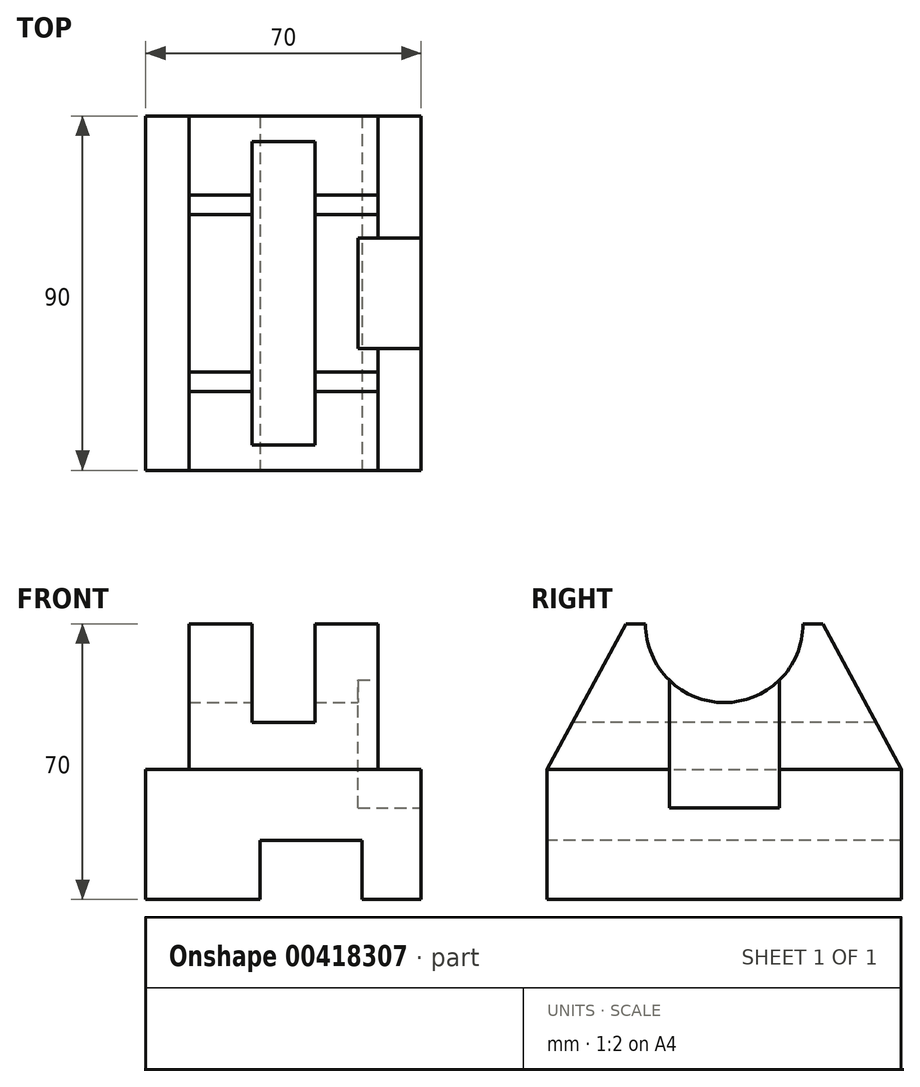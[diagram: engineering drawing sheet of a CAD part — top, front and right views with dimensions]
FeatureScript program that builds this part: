
annotation { "Feature Type Name" : "Feature", "Feature Type Description" : "" }
export const myFeature = defineFeature(function(context is Context, id is Id, definition is map)
    precondition{}
    {
        {
            var Q0;
            Q0=qCreatedBy(makeId("Right.planeOp"),FACE);
            var sketch = newSketch(context, id + "F0", { "sketchPlane" : qUnion([Q0])});
            skLineSegment(sketch, "E0", {"start": v(-45, 0) * mm, "end": v(45, 0) * mm});
            skLineSegment(sketch, "E1", {"start": v(45, 0) * mm, "end": v(25, 37) * mm});
            skLineSegment(sketch, "E2", {"start": v(25, 37) * mm, "end": v(-25, 37) * mm});
            skLineSegment(sketch, "E3", {"start": v(-25, 37) * mm, "end": v(-45, 0) * mm});
            skSolve(sketch);
        }
        {
            var Q0;
            Q0=qCreatedBy(makeId("Top.planeOp"),FACE);
            var sketch = newSketch(context, id + "F1", { "sketchPlane" : qUnion([Q0])});
            skLineSegment(sketch, "E4.bottom", {"start": v(-35, -45) * mm, "end": v(35, -45) * mm});
            skLineSegment(sketch, "E4.top", {"start": v(-35, 45) * mm, "end": v(35, 45) * mm});
            skLineSegment(sketch, "E4.left", {"start": v(-35, -45) * mm, "end": v(-35, 45) * mm});
            skLineSegment(sketch, "E4.right", {"start": v(35, -45) * mm, "end": v(35, 45) * mm});
            skPoint(sketch, "E4.middle", {"position": v(0, 0) * mm});
            skSolve(sketch);
        }
        {
            var Q0;
            Q0 = qSketchRegion(id + "F1", true);
            extrude(context, id + "F2", {"entities" : qUnion([Q0]), "oppositeDirection" : true, "depth" : 33 * mm});
        }
        {
            var Q0;
            Q0=makeQuery(id+"F2.opExtrude","SWEPT_FACE",FACE,{"disambiguationData":[OSD([sQuery(id+"F1.wireOp",EDGE,"E4.bottom")])]});
            var sketch = newSketch(context, id + "F3", { "sketchPlane" : qUnion([Q0])});
            skLineSegment(sketch, "E5.bottom", {"start": v(-6, -18) * mm, "end": v(20, -18) * mm});
            skLineSegment(sketch, "E5.top", {"start": v(-6, -33) * mm, "end": v(20, -33) * mm});
            skLineSegment(sketch, "E5.left", {"start": v(-6, -18) * mm, "end": v(-6, -33) * mm});
            skLineSegment(sketch, "E5.right", {"start": v(20, -18) * mm, "end": v(20, -33) * mm});
            skSolve(sketch);
        }
        {
            var Q0;
            Q0 = qSketchRegion(id + "F3", true);
            extrude(context, id + "F4", {"entities" : qUnion([Q0]), "operationType" : NewBodyOperationType.REMOVE, "endBound" : BoundingType.THROUGH_ALL, "oppositeDirection" : true, "depth" : 25 * mm});
        }
        {
            var Q0;
            Q0 = qSketchRegion(id + "F0", true);
            extrude(context, id + "F5", {"entities" : qUnion([Q0]), "operationType" : NewBodyOperationType.ADD, "endBound" : BoundingType.SYMMETRIC, "depth" : 48 * mm});
        }
        {
            var Q0;
            Q0=makeQuery(id+"F2.opExtrude","SWEPT_FACE",FACE,{"disambiguationData":[OSD([sQuery(id+"F1.wireOp",EDGE,"E4.bottom")])]});
            var sketch = newSketch(context, id + "F6", { "sketchPlane" : qUnion([Q0])});
            skLineSegment(sketch, "E6.bottom", {"start": v(-8, 37) * mm, "end": v(8, 37) * mm});
            skLineSegment(sketch, "E6.top", {"start": v(-8, 12) * mm, "end": v(8, 12) * mm});
            skLineSegment(sketch, "E6.left", {"start": v(-8, 37) * mm, "end": v(-8, 12) * mm});
            skLineSegment(sketch, "E6.right", {"start": v(8, 37) * mm, "end": v(8, 12) * mm});
            skSolve(sketch);
        }
        {
            var Q0;
            Q0 = qSketchRegion(id + "F6", true);
            extrude(context, id + "F7", {"entities" : qUnion([Q0]), "operationType" : NewBodyOperationType.REMOVE, "endBound" : BoundingType.THROUGH_ALL, "oppositeDirection" : true, "depth" : 25 * mm});
        }
        {
            var Q0;
            Q0=makeQuery(id+"F5.opExtrude","CAP_FACE",FACE,{"disambiguationData":[OSD([sQuery(id+"F0.wireOp",EDGE,"E0"),sQuery(id+"F0.wireOp",EDGE,"E1"),sQuery(id+"F0.wireOp",EDGE,"E2"),sQuery(id+"F0.wireOp",EDGE,"E3")])],"isStart":false});
            var sketch = newSketch(context, id + "F8", { "sketchPlane" : qUnion([Q0])});
            skCircle(sketch, "E7", {"center": v(0, 37) * mm, "radius": 20 * mm});
            skSolve(sketch);
        }
        {
            var Q0;
            Q0 = qSketchRegion(id + "F8", true);
            extrude(context, id + "F9", {"entities" : qUnion([Q0]), "operationType" : NewBodyOperationType.REMOVE, "endBound" : BoundingType.THROUGH_ALL, "oppositeDirection" : true, "depth" : 25 * mm});
        }
        {
            var Q0;
            Q0=makeQuery(id+"F2.opExtrude","SWEPT_FACE",FACE,{"disambiguationData":[OSD([sQuery(id+"F1.wireOp",EDGE,"E4.right")])]});
            var sketch = newSketch(context, id + "F10", { "sketchPlane" : qUnion([Q0])});
            skLineSegment(sketch, "E8.bottom", {"start": v(-14, -9.75) * mm, "end": v(14, -9.75) * mm});
            skLineSegment(sketch, "E8.top", {"start": v(-14, 40.25) * mm, "end": v(14, 40.25) * mm});
            skLineSegment(sketch, "E8.left", {"start": v(-14, -9.75) * mm, "end": v(-14, 40.25) * mm});
            skLineSegment(sketch, "E8.right", {"start": v(14, -9.75) * mm, "end": v(14, 40.25) * mm});
            skSolve(sketch);
        }
        {
            var Q0;
            Q0 = qSketchRegion(id + "F10", true);
            extrude(context, id + "F11", {"entities" : qUnion([Q0]), "operationType" : NewBodyOperationType.REMOVE, "oppositeDirection" : true, "depth" : 16 * mm});
        }
    });
